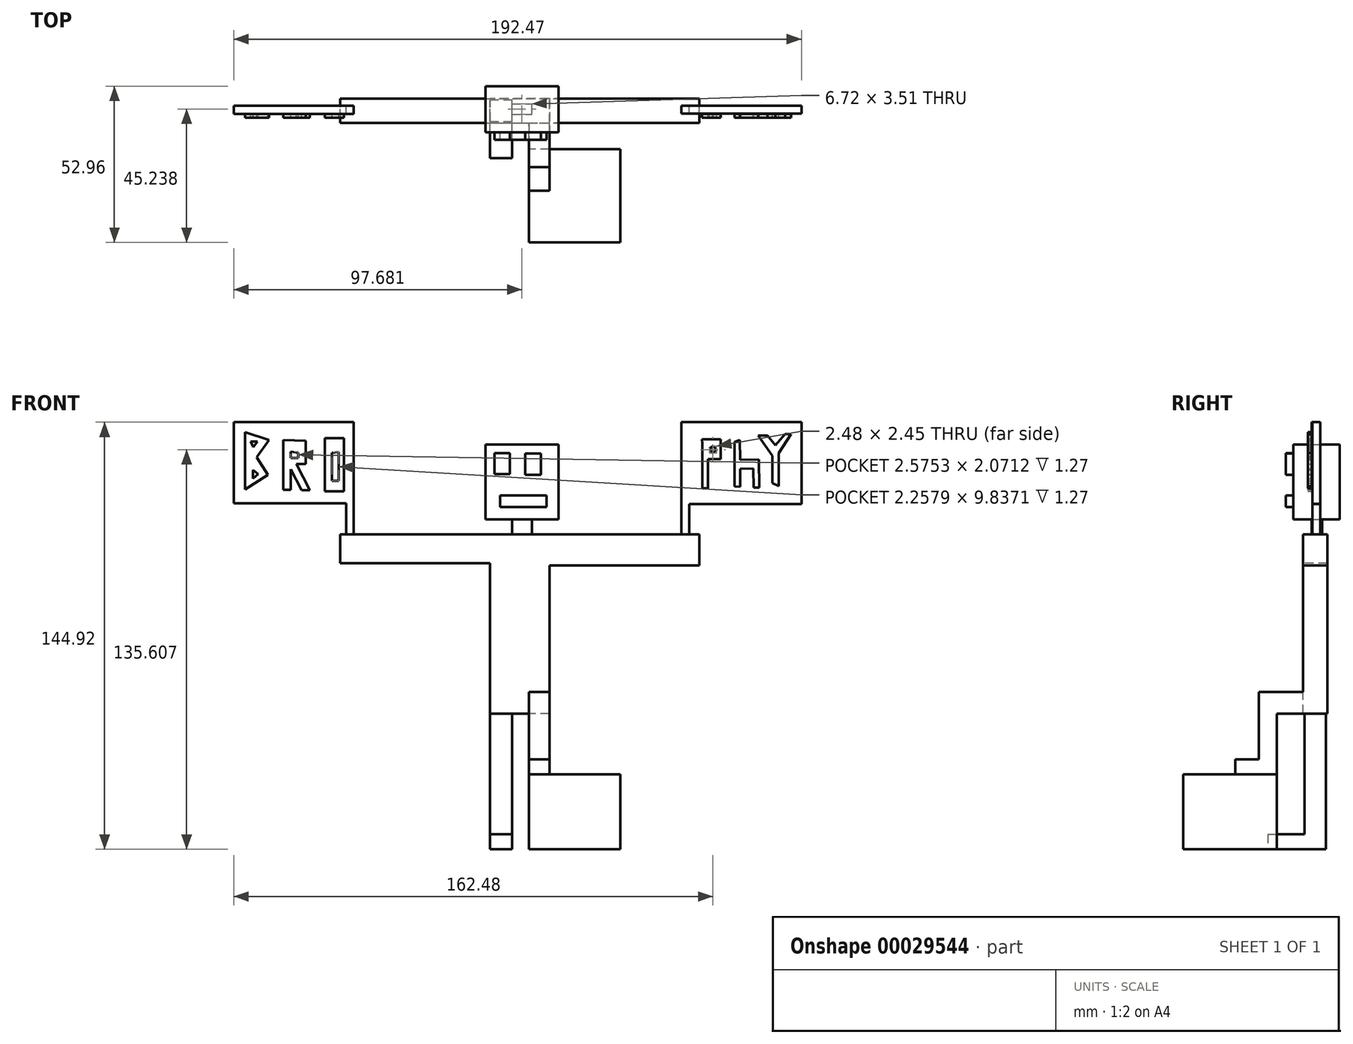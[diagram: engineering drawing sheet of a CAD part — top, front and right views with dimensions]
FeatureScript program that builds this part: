
annotation { "Feature Type Name" : "Feature", "Feature Type Description" : "" }
export const myFeature = defineFeature(function(context is Context, id is Id, definition is map)
    precondition{}
    {
        {
            var Q0;
            Q0=qCreatedBy(makeId("Top.planeOp"),FACE);
            var sketch = newSketch(context, id + "F0", { "sketchPlane" : qUnion([Q0])});
            skLineSegment(sketch, "E0.bottom", {"start": v(13.25, -35.71) * mm, "end": v(44.3, -35.71) * mm});
            skLineSegment(sketch, "E0.top", {"start": v(13.25, -4.04) * mm, "end": v(44.3, -4.04) * mm});
            skLineSegment(sketch, "E0.left", {"start": v(13.25, -35.71) * mm, "end": v(13.25, -4.04) * mm});
            skLineSegment(sketch, "E0.right", {"start": v(44.3, -35.71) * mm, "end": v(44.3, -4.04) * mm});
            skSolve(sketch);
        }
        {
            var Q0;
            Q0 = qSketchRegion(id + "F0", true);
            extrude(context, id + "F1", {"entities" : qUnion([Q0]), "depth" : 25.4 * mm});
        }
        {
            var Q0;
            Q0=qCreatedBy(makeId("Top.planeOp"),FACE);
            var sketch = newSketch(context, id + "F2", { "sketchPlane" : qUnion([Q0])});
            skLineSegment(sketch, "E1.bottom", {"start": v(0, -7.11) * mm, "end": v(7.59, -7.11) * mm});
            skLineSegment(sketch, "E1.top", {"start": v(0, 12.63) * mm, "end": v(7.59, 12.63) * mm});
            skLineSegment(sketch, "E1.left", {"start": v(0, -7.11) * mm, "end": v(0, 12.63) * mm});
            skLineSegment(sketch, "E1.right", {"start": v(7.59, -7.11) * mm, "end": v(7.59, 12.63) * mm});
            skSolve(sketch);
        }
        {
            var Q0;
            Q0 = qSketchRegion(id + "F2", true);
            extrude(context, id + "F3", {"entities" : qUnion([Q0]), "depth" : 5.08 * mm});
        }
        {
            var Q0;
            Q0=makeQuery(id+"F3.opExtrude","CAP_FACE",FACE,{"disambiguationData":[OSD([sQuery(id+"F2.wireOp",EDGE,"E1.bottom"),sQuery(id+"F2.wireOp",EDGE,"E1.top"),sQuery(id+"F2.wireOp",EDGE,"E1.left"),sQuery(id+"F2.wireOp",EDGE,"E1.right")])],"isStart":false});
            var sketch = newSketch(context, id + "F4", { "sketchPlane" : qUnion([Q0])});
            skLineSegment(sketch, "E2.bottom", {"start": v(0, 12.63) * mm, "end": v(7.59, 12.63) * mm});
            skLineSegment(sketch, "E2.top", {"start": v(0, 5.35) * mm, "end": v(7.59, 5.35) * mm});
            skLineSegment(sketch, "E2.left", {"start": v(0, 12.63) * mm, "end": v(0, 5.35) * mm});
            skLineSegment(sketch, "E2.right", {"start": v(7.59, 12.63) * mm, "end": v(7.59, 5.35) * mm});
            skSolve(sketch);
        }
        {
            var Q0;
            Q0 = qSketchRegion(id + "F4", true);
            extrude(context, id + "F5", {"entities" : qUnion([Q0]), "operationType" : NewBodyOperationType.ADD, "depth" : 40.64 * mm});
        }
        {
            var Q0;
            Q0=makeQuery(id+"F1.opExtrude","CAP_FACE",FACE,{"disambiguationData":[OSD([sQuery(id+"F0.wireOp",EDGE,"E0.bottom"),sQuery(id+"F0.wireOp",EDGE,"E0.top"),sQuery(id+"F0.wireOp",EDGE,"E0.left"),sQuery(id+"F0.wireOp",EDGE,"E0.right")])],"isStart":false});
            var sketch = newSketch(context, id + "F6", { "sketchPlane" : qUnion([Q0])});
            skLineSegment(sketch, "E3.bottom", {"start": v(13.25, -18.15) * mm, "end": v(20.2, -18.15) * mm});
            skLineSegment(sketch, "E3.top", {"start": v(13.25, -4.04) * mm, "end": v(20.2, -4.04) * mm});
            skLineSegment(sketch, "E3.left", {"start": v(13.25, -18.15) * mm, "end": v(13.25, -4.04) * mm});
            skLineSegment(sketch, "E3.right", {"start": v(20.2, -18.15) * mm, "end": v(20.2, -4.04) * mm});
            skSolve(sketch);
        }
        {
            var Q0;
            Q0 = qSketchRegion(id + "F6", true);
            extrude(context, id + "F7", {"entities" : qUnion([Q0]), "operationType" : NewBodyOperationType.ADD, "depth" : 5.08 * mm});
        }
        {
            var Q0;
            Q0=makeQuery(id+"F7.opExtrude","CAP_FACE",FACE,{"disambiguationData":[OSD([sQuery(id+"F6.wireOp",EDGE,"E3.bottom"),sQuery(id+"F6.wireOp",EDGE,"E3.top"),sQuery(id+"F6.wireOp",EDGE,"E3.left"),sQuery(id+"F6.wireOp",EDGE,"E3.right")])],"isStart":false});
            var sketch = newSketch(context, id + "F8", { "sketchPlane" : qUnion([Q0])});
            skLineSegment(sketch, "E4.bottom", {"start": v(13.25, -4.04) * mm, "end": v(20.2, -4.04) * mm});
            skLineSegment(sketch, "E4.top", {"start": v(13.25, -10.16) * mm, "end": v(20.2, -10.16) * mm});
            skLineSegment(sketch, "E4.left", {"start": v(13.25, -4.04) * mm, "end": v(13.25, -10.16) * mm});
            skLineSegment(sketch, "E4.right", {"start": v(20.2, -4.04) * mm, "end": v(20.2, -10.16) * mm});
            skSolve(sketch);
        }
        {
            var Q0;
            Q0 = qSketchRegion(id + "F8", true);
            extrude(context, id + "F9", {"entities" : qUnion([Q0]), "operationType" : NewBodyOperationType.ADD, "depth" : 22.86 * mm});
        }
        {
            var Q0;
            Q0=makeQuery(id+"F9.boolean.opBoolean","MERGE",FACE,{"derivedFrom":[makeQuery(id+"F7.boolean.opBoolean","MERGE",FACE,{"derivedFrom":[makeQuery(id+"F1.opExtrude","SWEPT_FACE",FACE,{"disambiguationData":[OSD([sQuery(id+"F0.wireOp",EDGE,"E0.top")])]}),makeQuery(id+"F7.opExtrude","SWEPT_FACE",FACE,{"disambiguationData":[OSD([sQuery(id+"F6.wireOp",EDGE,"E3.top")])]})]}),makeQuery(id+"F9.opExtrude","SWEPT_FACE",FACE,{"disambiguationData":[OSD([sQuery(id+"F8.wireOp",EDGE,"E4.bottom")])]})]});
            var sketch = newSketch(context, id + "F10", { "sketchPlane" : qUnion([Q0])});
            skLineSegment(sketch, "E5.bottom", {"start": v(-20.2, 53.34) * mm, "end": v(-13.25, 53.34) * mm});
            skLineSegment(sketch, "E5.top", {"start": v(-20.2, 46.06) * mm, "end": v(-13.25, 46.06) * mm});
            skLineSegment(sketch, "E5.left", {"start": v(-20.2, 53.34) * mm, "end": v(-20.2, 46.06) * mm});
            skLineSegment(sketch, "E5.right", {"start": v(-13.25, 53.34) * mm, "end": v(-13.25, 46.06) * mm});
            skSolve(sketch);
        }
        {
            var Q0;
            Q0 = qSketchRegion(id + "F10", true);
            extrude(context, id + "F11", {"entities" : qUnion([Q0]), "operationType" : NewBodyOperationType.ADD, "depth" : 17.1 * mm});
        }
        {
            var Q0;
            Q0=makeQuery(id+"F11.boolean.opBoolean","MERGE",FACE,{"derivedFrom":[makeQuery(id+"F9.boolean.opBoolean","MERGE",FACE,{"derivedFrom":[makeQuery(id+"F7.boolean.opBoolean","MERGE",FACE,{"derivedFrom":[makeQuery(id+"F1.opExtrude","SWEPT_FACE",FACE,{"disambiguationData":[OSD([sQuery(id+"F0.wireOp",EDGE,"E0.left")])]}),makeQuery(id+"F7.opExtrude","SWEPT_FACE",FACE,{"disambiguationData":[OSD([sQuery(id+"F6.wireOp",EDGE,"E3.left")])]})]}),makeQuery(id+"F9.opExtrude","SWEPT_FACE",FACE,{"disambiguationData":[OSD([sQuery(id+"F8.wireOp",EDGE,"E4.left")])]})]}),makeQuery(id+"F11.opExtrude","SWEPT_FACE",FACE,{"disambiguationData":[OSD([sQuery(id+"F10.wireOp",EDGE,"E5.right")])]})]});
            var sketch = newSketch(context, id + "F12", { "sketchPlane" : qUnion([Q0])});
            skLineSegment(sketch, "E6.bottom", {"start": v(-13.07, 46.06) * mm, "end": v(-4.86, 46.06) * mm});
            skLineSegment(sketch, "E6.top", {"start": v(-13.07, 53.34) * mm, "end": v(-4.86, 53.34) * mm});
            skLineSegment(sketch, "E6.left", {"start": v(-13.07, 46.06) * mm, "end": v(-13.07, 53.34) * mm});
            skLineSegment(sketch, "E6.right", {"start": v(-4.86, 46.06) * mm, "end": v(-4.86, 53.34) * mm});
            skSolve(sketch);
        }
        {
            var Q0;
            Q0 = qSketchRegion(id + "F12", true);
            extrude(context, id + "F13", {"entities" : qUnion([Q0]), "operationType" : NewBodyOperationType.ADD, "depth" : 13.2 * mm});
        }
        {
            var Q0;
            Q0=makeQuery(id+"F5.opExtrude","CAP_FACE",FACE,{"disambiguationData":[OSD([sQuery(id+"F4.wireOp",EDGE,"E2.bottom"),sQuery(id+"F4.wireOp",EDGE,"E2.top"),sQuery(id+"F4.wireOp",EDGE,"E2.left"),sQuery(id+"F4.wireOp",EDGE,"E2.right")])],"isStart":false});
            extrude(context, id + "F14", {"entities" : qUnion([Q0]), "operationType" : NewBodyOperationType.ADD, "depth" : 0.26 * mm});
        }
        {
            var Q0;
            Q0=makeQuery(id+"F13.boolean.opBoolean","MERGE",FACE,{"derivedFrom":[makeQuery(id+"F11.boolean.opBoolean","MERGE",FACE,{"derivedFrom":[makeQuery(id+"F9.opExtrude","CAP_FACE",FACE,{"disambiguationData":[OSD([sQuery(id+"F8.wireOp",EDGE,"E4.bottom"),sQuery(id+"F8.wireOp",EDGE,"E4.top"),sQuery(id+"F8.wireOp",EDGE,"E4.left"),sQuery(id+"F8.wireOp",EDGE,"E4.right")])],"isStart":false}),makeQuery(id+"F11.opExtrude","SWEPT_FACE",FACE,{"disambiguationData":[OSD([sQuery(id+"F10.wireOp",EDGE,"E5.bottom")])]})]}),makeQuery(id+"F13.opExtrude","SWEPT_FACE",FACE,{"disambiguationData":[OSD([sQuery(id+"F12.wireOp",EDGE,"E6.top")])]})]});
            var sketch = newSketch(context, id + "F15", { "sketchPlane" : qUnion([Q0])});
            skLineSegment(sketch, "E7.bottom", {"start": v(0.06, 4.86) * mm, "end": v(20.2, 4.86) * mm});
            skLineSegment(sketch, "E7.top", {"start": v(0.06, 13.07) * mm, "end": v(20.2, 13.07) * mm});
            skLineSegment(sketch, "E7.left", {"start": v(0.06, 4.86) * mm, "end": v(0.06, 13.07) * mm});
            skLineSegment(sketch, "E7.right", {"start": v(20.2, 4.86) * mm, "end": v(20.2, 13.07) * mm});
            skSolve(sketch);
        }
        {
            var Q0;
            Q0 = qSketchRegion(id + "F15", true);
            extrude(context, id + "F16", {"entities" : qUnion([Q0]), "operationType" : NewBodyOperationType.ADD, "depth" : 53.48 * mm});
        }
        {
            var Q0;
            Q0=makeQuery(id+"F16.boolean.opBoolean","MERGE",FACE,{"derivedFrom":[makeQuery(id+"F11.boolean.opBoolean","MERGE",FACE,{"derivedFrom":[makeQuery(id+"F9.boolean.opBoolean","MERGE",FACE,{"derivedFrom":[makeQuery(id+"F7.opExtrude","SWEPT_FACE",FACE,{"disambiguationData":[OSD([sQuery(id+"F6.wireOp",EDGE,"E3.right")])]}),makeQuery(id+"F9.opExtrude","SWEPT_FACE",FACE,{"disambiguationData":[OSD([sQuery(id+"F8.wireOp",EDGE,"E4.right")])]})]}),makeQuery(id+"F11.opExtrude","SWEPT_FACE",FACE,{"disambiguationData":[OSD([sQuery(id+"F10.wireOp",EDGE,"E5.left")])]})]}),makeQuery(id+"F16.opExtrude","SWEPT_FACE",FACE,{"disambiguationData":[OSD([sQuery(id+"F15.wireOp",EDGE,"E7.right")])]})]});
            var sketch = newSketch(context, id + "F17", { "sketchPlane" : qUnion([Q0])});
            skLineSegment(sketch, "E8.bottom", {"start": v(4.86, 106.82) * mm, "end": v(13.07, 106.82) * mm});
            skLineSegment(sketch, "E8.top", {"start": v(4.86, 96.3) * mm, "end": v(13.07, 96.3) * mm});
            skLineSegment(sketch, "E8.left", {"start": v(4.86, 106.82) * mm, "end": v(4.86, 96.3) * mm});
            skLineSegment(sketch, "E8.right", {"start": v(13.07, 106.82) * mm, "end": v(13.07, 96.3) * mm});
            skSolve(sketch);
        }
        {
            var Q0;
            Q0 = qSketchRegion(id + "F17", true);
            extrude(context, id + "F18", {"entities" : qUnion([Q0]), "operationType" : NewBodyOperationType.ADD, "depth" : 50.8 * mm});
        }
        {
            var Q0;
            Q0=makeQuery(id+"F16.boolean.opBoolean","MERGE",FACE,{"derivedFrom":[makeQuery(id+"F13.opExtrude","CAP_FACE",FACE,{"disambiguationData":[OSD([sQuery(id+"F12.wireOp",EDGE,"E6.bottom"),sQuery(id+"F12.wireOp",EDGE,"E6.top"),sQuery(id+"F12.wireOp",EDGE,"E6.left"),sQuery(id+"F12.wireOp",EDGE,"E6.right")])],"isStart":false}),makeQuery(id+"F16.opExtrude","SWEPT_FACE",FACE,{"disambiguationData":[OSD([sQuery(id+"F15.wireOp",EDGE,"E7.left")])]})]});
            var sketch = newSketch(context, id + "F19", { "sketchPlane" : qUnion([Q0])});
            skLineSegment(sketch, "E9.bottom", {"start": v(-13.07, 106.82) * mm, "end": v(-4.86, 106.82) * mm});
            skLineSegment(sketch, "E9.top", {"start": v(-13.07, 97.1) * mm, "end": v(-4.86, 97.1) * mm});
            skLineSegment(sketch, "E9.left", {"start": v(-13.07, 106.82) * mm, "end": v(-13.07, 97.1) * mm});
            skLineSegment(sketch, "E9.right", {"start": v(-4.86, 106.82) * mm, "end": v(-4.86, 97.1) * mm});
            skSolve(sketch);
        }
        {
            var Q0;
            Q0 = qSketchRegion(id + "F19", true);
            extrude(context, id + "F20", {"entities" : qUnion([Q0]), "operationType" : NewBodyOperationType.ADD, "depth" : 50.8 * mm});
        }
        {
            var Q0;
            Q0=makeQuery(id+"F20.boolean.opBoolean","MERGE",FACE,{"derivedFrom":[makeQuery(id+"F18.boolean.opBoolean","MERGE",FACE,{"derivedFrom":[makeQuery(id+"F16.opExtrude","CAP_FACE",FACE,{"disambiguationData":[OSD([sQuery(id+"F15.wireOp",EDGE,"E7.bottom"),sQuery(id+"F15.wireOp",EDGE,"E7.top"),sQuery(id+"F15.wireOp",EDGE,"E7.left"),sQuery(id+"F15.wireOp",EDGE,"E7.right")])],"isStart":false}),makeQuery(id+"F18.opExtrude","SWEPT_FACE",FACE,{"disambiguationData":[OSD([sQuery(id+"F17.wireOp",EDGE,"E8.bottom")])]})]}),makeQuery(id+"F20.opExtrude","SWEPT_FACE",FACE,{"disambiguationData":[OSD([sQuery(id+"F19.wireOp",EDGE,"E9.bottom")])]})]});
            var sketch = newSketch(context, id + "F21", { "sketchPlane" : qUnion([Q0])});
            skLineSegment(sketch, "E10.bottom", {"start": v(67.58, 8.01) * mm, "end": v(64.92, 8.01) * mm});
            skLineSegment(sketch, "E10.top", {"start": v(67.58, 10.68) * mm, "end": v(64.92, 10.68) * mm});
            skLineSegment(sketch, "E10.left", {"start": v(67.58, 8.01) * mm, "end": v(67.58, 10.68) * mm});
            skLineSegment(sketch, "E10.right", {"start": v(64.92, 8.01) * mm, "end": v(64.92, 10.68) * mm});
            skLineSegment(sketch, "E11.bottom", {"start": v(-46.1, 7.8) * mm, "end": v(-48.7, 7.8) * mm});
            skLineSegment(sketch, "E11.top", {"start": v(-46.1, 10.61) * mm, "end": v(-48.7, 10.61) * mm});
            skLineSegment(sketch, "E11.left", {"start": v(-46.1, 7.8) * mm, "end": v(-46.1, 10.61) * mm});
            skLineSegment(sketch, "E11.right", {"start": v(-48.7, 7.8) * mm, "end": v(-48.7, 10.61) * mm});
            skSolve(sketch);
        }
        {
            var Q0;
            Q0=makeQuery(id+"F20.boolean.opBoolean","MERGE",FACE,{"derivedFrom":[makeQuery(id+"F18.boolean.opBoolean","MERGE",FACE,{"derivedFrom":[makeQuery(id+"F16.opExtrude","CAP_FACE",FACE,{"disambiguationData":[OSD([sQuery(id+"F15.wireOp",EDGE,"E7.bottom"),sQuery(id+"F15.wireOp",EDGE,"E7.top"),sQuery(id+"F15.wireOp",EDGE,"E7.left"),sQuery(id+"F15.wireOp",EDGE,"E7.right")])],"isStart":false}),makeQuery(id+"F18.opExtrude","SWEPT_FACE",FACE,{"disambiguationData":[OSD([sQuery(id+"F17.wireOp",EDGE,"E8.bottom")])]})]}),makeQuery(id+"F20.opExtrude","SWEPT_FACE",FACE,{"disambiguationData":[OSD([sQuery(id+"F19.wireOp",EDGE,"E9.bottom")])]})]});
            var sketch = newSketch(context, id + "F22", { "sketchPlane" : qUnion([Q0])});
            skLineSegment(sketch, "E12.bottom", {"start": v(7.53, 7.77) * mm, "end": v(14.25, 7.77) * mm});
            skLineSegment(sketch, "E12.top", {"start": v(7.53, 11.28) * mm, "end": v(14.25, 11.28) * mm});
            skLineSegment(sketch, "E12.left", {"start": v(7.53, 7.77) * mm, "end": v(7.53, 11.28) * mm});
            skLineSegment(sketch, "E12.right", {"start": v(14.25, 7.77) * mm, "end": v(14.25, 11.28) * mm});
            skSolve(sketch);
        }
        {
            var Q0;
            Q0 = qSketchRegion(id + "F22", true);
            extrude(context, id + "F23", {"entities" : qUnion([Q0]), "operationType" : NewBodyOperationType.ADD, "depth" : 5.08 * mm});
        }
        {
            var Q0;
            Q0=makeQuery(id+"F23.opExtrude","CAP_FACE",FACE,{"disambiguationData":[OSD([sQuery(id+"F22.wireOp",EDGE,"E12.bottom"),sQuery(id+"F22.wireOp",EDGE,"E12.top"),sQuery(id+"F22.wireOp",EDGE,"E12.left"),sQuery(id+"F22.wireOp",EDGE,"E12.right")])],"isStart":false});
            var sketch = newSketch(context, id + "F24", { "sketchPlane" : qUnion([Q0])});
            skLineSegment(sketch, "E13.rect.bottom", {"start": v(23.31, 1.6) * mm, "end": v(-1.5, 1.6) * mm});
            skLineSegment(sketch, "E13.rect.top", {"start": v(23.31, 17.25) * mm, "end": v(-1.5, 17.25) * mm});
            skLineSegment(sketch, "E13.rect.left", {"start": v(23.31, 1.6) * mm, "end": v(23.31, 17.25) * mm});
            skLineSegment(sketch, "E13.rect.right", {"start": v(-1.5, 1.6) * mm, "end": v(-1.5, 17.25) * mm});
            skPoint(sketch, "E13.rect.middle", {"position": v(10.9, 9.42) * mm});
            skSolve(sketch);
        }
        {
            var Q0;
            Q0 = qSketchRegion(id + "F24", true);
            extrude(context, id + "F25", {"entities" : qUnion([Q0]), "operationType" : NewBodyOperationType.ADD, "depth" : 25.4 * mm});
        }
        {
            var Q0;
            Q0=makeQuery(id+"F25.opExtrude","SWEPT_FACE",FACE,{"disambiguationData":[OSD([sQuery(id+"F24.wireOp",EDGE,"E13.rect.bottom")])]});
            var sketch = newSketch(context, id + "F26", { "sketchPlane" : qUnion([Q0])});
            skLineSegment(sketch, "E14.rect.bottom", {"start": v(6.86, 127.32) * mm, "end": v(1.62, 127.32) * mm});
            skLineSegment(sketch, "E14.rect.top", {"start": v(6.86, 134.4) * mm, "end": v(1.62, 134.4) * mm});
            skLineSegment(sketch, "E14.rect.left", {"start": v(6.86, 127.32) * mm, "end": v(6.86, 134.4) * mm});
            skLineSegment(sketch, "E14.rect.right", {"start": v(1.62, 127.32) * mm, "end": v(1.62, 134.4) * mm});
            skPoint(sketch, "E14.rect.middle", {"position": v(4.24, 130.86) * mm});
            skLineSegment(sketch, "E15.rect.bottom", {"start": v(17.37, 127.06) * mm, "end": v(12, 127.06) * mm});
            skLineSegment(sketch, "E15.rect.top", {"start": v(17.37, 134.34) * mm, "end": v(12, 134.34) * mm});
            skLineSegment(sketch, "E15.rect.left", {"start": v(17.37, 127.06) * mm, "end": v(17.37, 134.34) * mm});
            skLineSegment(sketch, "E15.rect.right", {"start": v(12, 127.06) * mm, "end": v(12, 134.34) * mm});
            skPoint(sketch, "E15.rect.middle", {"position": v(14.69, 130.7) * mm});
            skSolve(sketch);
        }
        {
            var Q0;
            Q0 = qSketchRegion(id + "F26", true);
            extrude(context, id + "F27", {"entities" : qUnion([Q0]), "operationType" : NewBodyOperationType.ADD, "depth" : 2.54 * mm});
        }
        {
            var Q0;
            Q0 = qSketchRegion(id + "F21", true);
            extrude(context, id + "F28", {"entities" : qUnion([Q0]), "operationType" : NewBodyOperationType.ADD, "depth" : 38.1 * mm});
        }
        {
            var Q0;
            Q0=makeQuery(id+"F28.opExtrude","SWEPT_FACE",FACE,{"disambiguationData":[OSD([sQuery(id+"F21.wireOp",EDGE,"E10.left")])]});
            var sketch = newSketch(context, id + "F29", { "sketchPlane" : qUnion([Q0])});
            skLineSegment(sketch, "E16.bottom", {"start": v(8.01, 144.92) * mm, "end": v(10.68, 144.92) * mm});
            skLineSegment(sketch, "E16.top", {"start": v(8.01, 117.14) * mm, "end": v(10.68, 117.14) * mm});
            skLineSegment(sketch, "E16.left", {"start": v(8.01, 144.92) * mm, "end": v(8.01, 117.14) * mm});
            skLineSegment(sketch, "E16.right", {"start": v(10.68, 144.92) * mm, "end": v(10.68, 117.14) * mm});
            skSolve(sketch);
        }
        {
            var Q0;
            Q0 = qSketchRegion(id + "F29", true);
            extrude(context, id + "F30", {"entities" : qUnion([Q0]), "operationType" : NewBodyOperationType.ADD, "depth" : 38.1 * mm});
        }
        {
            var Q0;
            Q0=makeQuery(id+"F28.opExtrude","SWEPT_FACE",FACE,{"disambiguationData":[OSD([sQuery(id+"F21.wireOp",EDGE,"E11.right")])]});
            var sketch = newSketch(context, id + "F31", { "sketchPlane" : qUnion([Q0])});
            skLineSegment(sketch, "E17.bottom", {"start": v(-10.61, 144.92) * mm, "end": v(-7.8, 144.92) * mm});
            skLineSegment(sketch, "E17.top", {"start": v(-10.61, 117.37) * mm, "end": v(-7.8, 117.37) * mm});
            skLineSegment(sketch, "E17.left", {"start": v(-10.61, 144.92) * mm, "end": v(-10.61, 117.37) * mm});
            skLineSegment(sketch, "E17.right", {"start": v(-7.8, 144.92) * mm, "end": v(-7.8, 117.37) * mm});
            skSolve(sketch);
        }
        {
            var Q0;
            Q0 = qSketchRegion(id + "F31", true);
            extrude(context, id + "F32", {"entities" : qUnion([Q0]), "operationType" : NewBodyOperationType.ADD, "depth" : 38.1 * mm});
        }
        {
            var Q0;
            Q0=makeQuery(id+"F32.boolean.opBoolean","MERGE",FACE,{"derivedFrom":[makeQuery(id+"F28.opExtrude","SWEPT_FACE",FACE,{"disambiguationData":[OSD([sQuery(id+"F21.wireOp",EDGE,"E11.bottom")])]}),makeQuery(id+"F32.opExtrude","SWEPT_FACE",FACE,{"disambiguationData":[OSD([sQuery(id+"F31.wireOp",EDGE,"E17.right")])]})]});
            var sketch = newSketch(context, id + "F33", { "sketchPlane" : qUnion([Q0])});
            skLineSegment(sketch, "E18", {"start": v(-82.98, 141.52) * mm, "end": v(-82.98, 122.08) * mm});
            skLineSegment(sketch, "E19", {"start": v(-82.98, 122.08) * mm, "end": v(-75.23, 127.1) * mm});
            skLineSegment(sketch, "E20", {"start": v(-75.23, 127.1) * mm, "end": v(-79.05, 133) * mm});
            skLineSegment(sketch, "E21", {"start": v(-79.05, 133) * mm, "end": v(-74.86, 138.82) * mm});
            skLineSegment(sketch, "E22", {"start": v(-74.86, 138.82) * mm, "end": v(-82.98, 141.52) * mm});
            skLineSegment(sketch, "E23", {"start": v(-70.07, 138.82) * mm, "end": v(-70.07, 122) * mm});
            skLineSegment(sketch, "E24", {"start": v(-70.07, 122) * mm, "end": v(-67.44, 122) * mm});
            skLineSegment(sketch, "E25", {"start": v(-67.44, 122) * mm, "end": v(-67.44, 129.02) * mm});
            skLineSegment(sketch, "E26", {"start": v(-67.44, 129.02) * mm, "end": v(-63.8, 121.82) * mm});
            skLineSegment(sketch, "E27", {"start": v(-63.8, 121.82) * mm, "end": v(-61.09, 121.82) * mm});
            skLineSegment(sketch, "E28", {"start": v(-61.09, 121.82) * mm, "end": v(-65.65, 130.7) * mm});
            skLineSegment(sketch, "E29", {"start": v(-65.65, 130.7) * mm, "end": v(-62.47, 130.7) * mm});
            skLineSegment(sketch, "E30", {"start": v(-62.47, 130.7) * mm, "end": v(-62.47, 138.57) * mm});
            skLineSegment(sketch, "E31", {"start": v(-62.47, 138.57) * mm, "end": v(-70.07, 138.82) * mm});
            skLineSegment(sketch, "E32", {"start": v(-55.9, 138.57) * mm, "end": v(-55.9, 121.47) * mm});
            skLineSegment(sketch, "E33", {"start": v(-55.9, 121.47) * mm, "end": v(-49.42, 121.47) * mm});
            skLineSegment(sketch, "E34", {"start": v(-49.42, 121.47) * mm, "end": v(-49.42, 139.56) * mm});
            skLineSegment(sketch, "E35", {"start": v(-49.42, 139.56) * mm, "end": v(-55.9, 139.56) * mm});
            skLineSegment(sketch, "E36", {"start": v(-55.9, 139.56) * mm, "end": v(-55.9, 138.57) * mm});
            skLineSegment(sketch, "E37", {"start": v(-80.25, 136.41) * mm, "end": v(-78.86, 138.36) * mm});
            skLineSegment(sketch, "E38", {"start": v(-78.86, 138.36) * mm, "end": v(-81.09, 138.36) * mm});
            skLineSegment(sketch, "E39", {"start": v(-81.09, 138.36) * mm, "end": v(-80.25, 136.41) * mm});
            skLineSegment(sketch, "E40", {"start": v(-80.37, 128.7) * mm, "end": v(-80.37, 125.78) * mm});
            skLineSegment(sketch, "E41", {"start": v(-80.37, 125.78) * mm, "end": v(-78.57, 127.26) * mm});
            skLineSegment(sketch, "E42", {"start": v(-78.57, 127.26) * mm, "end": v(-80.37, 128.7) * mm});
            skLineSegment(sketch, "E43", {"start": v(-67.5, 134.9) * mm, "end": v(-67.5, 132.83) * mm});
            skLineSegment(sketch, "E44", {"start": v(-67.5, 132.83) * mm, "end": v(-64.92, 132.83) * mm});
            skLineSegment(sketch, "E45", {"start": v(-64.92, 132.83) * mm, "end": v(-64.92, 134.57) * mm});
            skLineSegment(sketch, "E46", {"start": v(-64.92, 134.57) * mm, "end": v(-67.5, 134.9) * mm});
            skLineSegment(sketch, "E47", {"start": v(-53.48, 134.57) * mm, "end": v(-53.48, 124.96) * mm});
            skLineSegment(sketch, "E48", {"start": v(-53.48, 124.96) * mm, "end": v(-51.22, 124.96) * mm});
            skLineSegment(sketch, "E49", {"start": v(-51.22, 124.96) * mm, "end": v(-51.22, 134.8) * mm});
            skLineSegment(sketch, "E50", {"start": v(-51.22, 134.8) * mm, "end": v(-53.48, 134.57) * mm});
            skLineSegment(sketch, "E51", {"start": v(72.09, 137.64) * mm, "end": v(72.09, 122.48) * mm});
            skLineSegment(sketch, "E52", {"start": v(72.09, 122.48) * mm, "end": v(73.96, 122.48) * mm});
            skLineSegment(sketch, "E53", {"start": v(73.96, 122.48) * mm, "end": v(73.96, 132.39) * mm});
            skLineSegment(sketch, "E54", {"start": v(73.96, 132.39) * mm, "end": v(78.3, 132.39) * mm});
            skLineSegment(sketch, "E55", {"start": v(78.3, 132.39) * mm, "end": v(78.3, 139.18) * mm});
            skLineSegment(sketch, "E56", {"start": v(78.3, 139.18) * mm, "end": v(71.9, 139.18) * mm});
            skLineSegment(sketch, "E57", {"start": v(71.9, 139.18) * mm, "end": v(72.09, 137.64) * mm});
            skLineSegment(sketch, "E58", {"start": v(74.45, 135.88) * mm, "end": v(75.54, 134.38) * mm});
            skLineSegment(sketch, "E59", {"start": v(75.54, 134.38) * mm, "end": v(76.93, 135.4) * mm});
            skLineSegment(sketch, "E60", {"start": v(76.93, 135.4) * mm, "end": v(75.88, 136.83) * mm});
            skLineSegment(sketch, "E61", {"start": v(75.88, 136.83) * mm, "end": v(74.45, 135.88) * mm});
            skLineSegment(sketch, "E62", {"start": v(82.98, 138.25) * mm, "end": v(82.98, 123.05) * mm});
            skLineSegment(sketch, "E63", {"start": v(82.98, 123.05) * mm, "end": v(84.85, 122.97) * mm});
            skLineSegment(sketch, "E64", {"start": v(84.85, 122.97) * mm, "end": v(84.85, 129.05) * mm});
            skLineSegment(sketch, "E65", {"start": v(84.85, 129.05) * mm, "end": v(89.29, 129.2) * mm});
            skLineSegment(sketch, "E66", {"start": v(89.29, 129.2) * mm, "end": v(89.52, 122.68) * mm});
            skLineSegment(sketch, "E67", {"start": v(89.52, 122.68) * mm, "end": v(91.41, 122.75) * mm});
            skLineSegment(sketch, "E68", {"start": v(91.41, 122.75) * mm, "end": v(91.3, 132.23) * mm});
            skLineSegment(sketch, "E69", {"start": v(91.3, 132.23) * mm, "end": v(84.87, 132.14) * mm});
            skLineSegment(sketch, "E70", {"start": v(84.87, 132.14) * mm, "end": v(84.78, 138.84) * mm});
            skLineSegment(sketch, "E71", {"start": v(84.78, 138.84) * mm, "end": v(82.98, 138.25) * mm});
            skLineSegment(sketch, "E72", {"start": v(95.78, 124.2) * mm, "end": v(95.78, 133.53) * mm});
            skLineSegment(sketch, "E73", {"start": v(95.78, 133.53) * mm, "end": v(90.97, 140.4) * mm});
            skLineSegment(sketch, "E74", {"start": v(90.97, 140.4) * mm, "end": v(94.22, 140.4) * mm});
            skLineSegment(sketch, "E75", {"start": v(94.22, 140.4) * mm, "end": v(96.8, 137.08) * mm});
            skLineSegment(sketch, "E76", {"start": v(96.8, 137.08) * mm, "end": v(100.17, 140.94) * mm});
            skLineSegment(sketch, "E77", {"start": v(100.17, 140.94) * mm, "end": v(102.2, 140.94) * mm});
            skLineSegment(sketch, "E78", {"start": v(102.2, 140.94) * mm, "end": v(97.93, 134.37) * mm});
            skLineSegment(sketch, "E79", {"start": v(97.93, 134.37) * mm, "end": v(97.93, 123.24) * mm});
            skLineSegment(sketch, "E80", {"start": v(97.93, 123.24) * mm, "end": v(95.78, 124.2) * mm});
            skSolve(sketch);
        }
        {
            var Q0;
            Q0 = qSketchRegion(id + "F33", true);
            extrude(context, id + "F34", {"entities" : qUnion([Q0]), "operationType" : NewBodyOperationType.ADD, "depth" : 1.27 * mm});
        }
        {
            var Q0;
            Q0=makeQuery(id+"F25.opExtrude","SWEPT_FACE",FACE,{"disambiguationData":[OSD([sQuery(id+"F24.wireOp",EDGE,"E13.rect.bottom")])]});
            var sketch = newSketch(context, id + "F35", { "sketchPlane" : qUnion([Q0])});
            skLineSegment(sketch, "E81.bottom", {"start": v(3.44, 116.13) * mm, "end": v(19.2, 116.13) * mm});
            skLineSegment(sketch, "E81.top", {"start": v(3.44, 120.05) * mm, "end": v(19.2, 120.05) * mm});
            skLineSegment(sketch, "E81.left", {"start": v(3.44, 116.13) * mm, "end": v(3.44, 120.05) * mm});
            skLineSegment(sketch, "E81.right", {"start": v(19.2, 116.13) * mm, "end": v(19.2, 120.05) * mm});
            skSolve(sketch);
        }
        {
            var Q0;
            Q0 = qSketchRegion(id + "F35", true);
            extrude(context, id + "F36", {"entities" : qUnion([Q0]), "operationType" : NewBodyOperationType.ADD, "depth" : 2.54 * mm});
        }
    });
